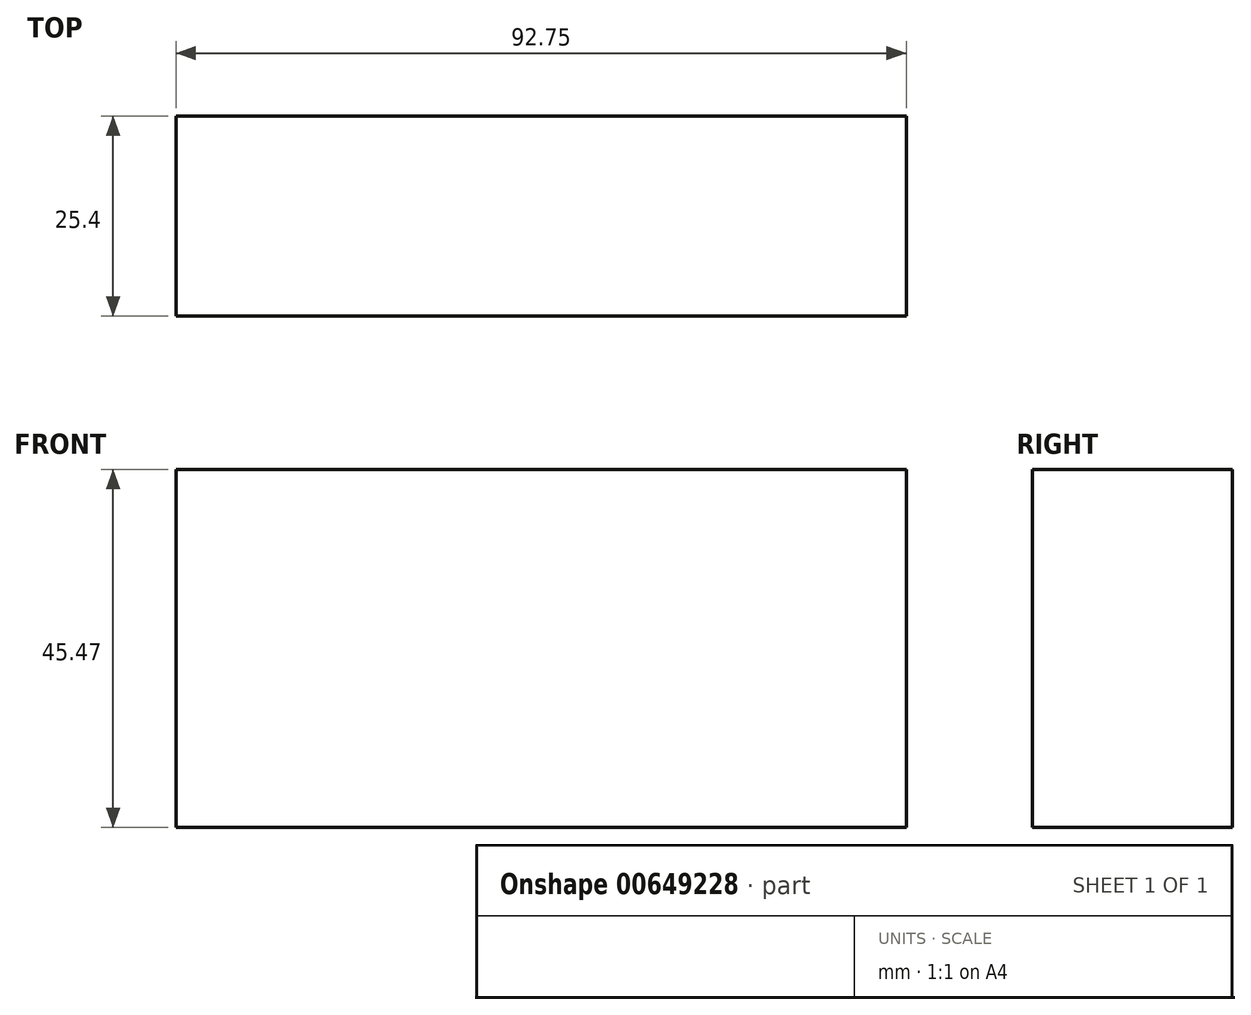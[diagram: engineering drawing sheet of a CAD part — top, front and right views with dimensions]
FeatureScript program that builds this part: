
annotation { "Feature Type Name" : "Feature", "Feature Type Description" : "" }
export const myFeature = defineFeature(function(context is Context, id is Id, definition is map)
    precondition{}
    {
        {
            var Q0;
            Q0=qCreatedBy(makeId("Front.planeOp"),FACE);
            var sketch = newSketch(context, id + "F0", { "sketchPlane" : qUnion([Q0])});
            skLineSegment(sketch, "E0.bottom", {"start": v(-39.79, -13.7) * mm, "end": v(52.96, -13.7) * mm});
            skLineSegment(sketch, "E0.top", {"start": v(-39.79, 31.78) * mm, "end": v(52.96, 31.78) * mm});
            skLineSegment(sketch, "E0.left", {"start": v(-39.79, -13.7) * mm, "end": v(-39.79, 31.78) * mm});
            skLineSegment(sketch, "E0.right", {"start": v(52.96, -13.7) * mm, "end": v(52.96, 31.78) * mm});
            skLineSegment(sketch, "E1.bottom", {"start": v(-39.79, -13.7) * mm, "end": v(-46.11, -13.7) * mm});
            skLineSegment(sketch, "E1.top", {"start": v(-39.79, -19.71) * mm, "end": v(-46.11, -19.71) * mm});
            skLineSegment(sketch, "E1.left", {"start": v(-39.79, -13.7) * mm, "end": v(-39.79, -19.71) * mm});
            skLineSegment(sketch, "E1.right", {"start": v(-46.11, -13.7) * mm, "end": v(-46.11, -19.71) * mm});
            skSolve(sketch);
        }
        {
            var Q0;
            Q0=makeQuery(id+"F0.imprint","IMPRINT",FACE,{"disambiguationData":[TD([[makeQuery(id+"F0.imprint","IMPRINT",EDGE,{"derivedFrom":sQuery(id+"F0.wireOp",EDGE,"E0.bottom")}),1.0]])]});
            extrude(context, id + "F1", {"entities" : qUnion([Q0]), "depth" : 25.4 * mm, "offsetDistance" : 25.4 * mm});
        }
    });
